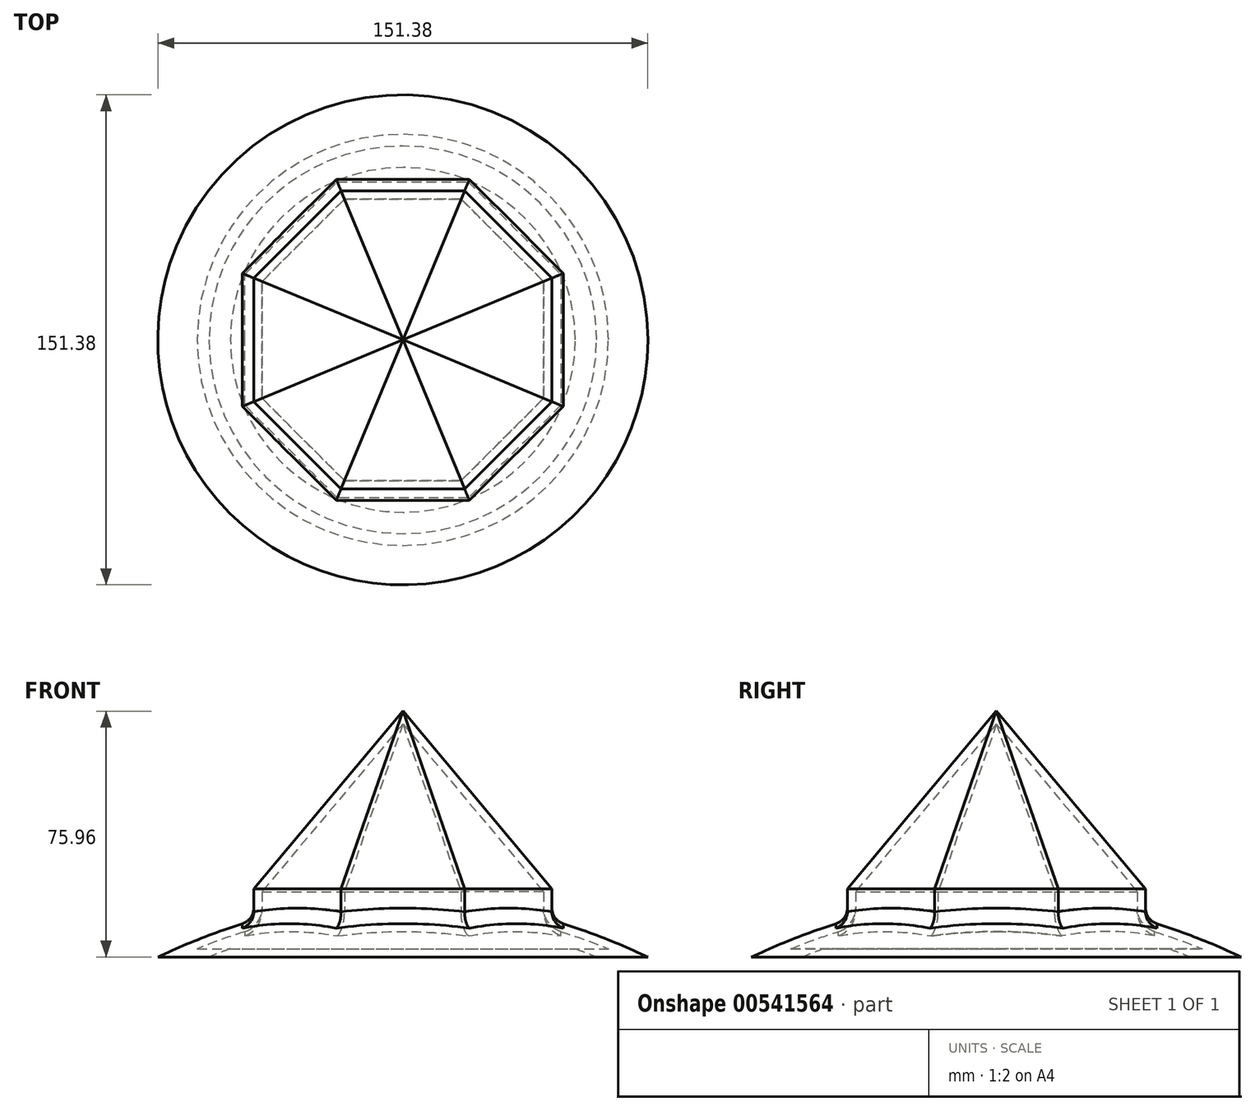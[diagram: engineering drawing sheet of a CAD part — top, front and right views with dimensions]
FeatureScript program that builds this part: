
annotation { "Feature Type Name" : "Feature", "Feature Type Description" : "" }
export const myFeature = defineFeature(function(context is Context, id is Id, definition is map)
    precondition{}
    {
        {
            var Q0;
            Q0=qCreatedBy(makeId("Front.planeOp"),FACE);
            var sketch = newSketch(context, id + "F0", { "sketchPlane" : qUnion([Q0])});
            skArc(sketch, "E0", {"start": v(0, 19.86) * mm, "mid": v(-38.76, 13.4) * mm, "end": v(-75.7, 0) * mm});
            skArc(sketch, "E1", {"start": v(0, 12.95) * mm, "mid": v(-30.5, 9.1) * mm, "end": v(-59.86, 0) * mm});
            skLineSegment(sketch, "E2", {"start": v(-75.7, 0) * mm, "end": v(-59.86, 0) * mm});
            skLineSegment(sketch, "E3", {"start": v(0, 19.86) * mm, "end": v(0, 12.95) * mm});
            skSolve(sketch);
        }
        {
            var Q0;
            Q0=makeQuery(id+"F0.imprint","IMPRINT",FACE,{"disambiguationData":[TD([[makeQuery(id+"F0.imprint","IMPRINT",EDGE,{"derivedFrom":sQuery(id+"F0.wireOp",EDGE,"E0")}),1.0]])]});
            var Q1;
            Q1=sQuery(id+"F0.wireOp",EDGE,"E3");
            revolve(context, id + "F1", {"entities" : qUnion([Q0]), "axis" : qUnion([Q1]), "revolveType" : RevolveType.FULL});
        }
        {
            var Q0;
            Q0=qCreatedBy(makeId("Top.planeOp"),FACE);
            var sketch = newSketch(context, id + "F2", { "sketchPlane" : qUnion([Q0])});
            skCircle(sketch, "E4.cCircle", {"center": v(0, 0) * mm, "radius": 46.05 * mm, "construction": true});
            skLineSegment(sketch, "E4.0", {"start": v(-19.07, 46.05) * mm, "end": v(19.07, 46.05) * mm});
            skLineSegment(sketch, "E4.1", {"start": v(19.07, 46.05) * mm, "end": v(46.05, 19.07) * mm});
            skLineSegment(sketch, "E4.2", {"start": v(46.05, 19.07) * mm, "end": v(46.05, -19.07) * mm});
            skLineSegment(sketch, "E4.3", {"start": v(46.05, -19.07) * mm, "end": v(19.07, -46.05) * mm});
            skLineSegment(sketch, "E4.4", {"start": v(19.07, -46.05) * mm, "end": v(-19.07, -46.05) * mm});
            skLineSegment(sketch, "E4.5", {"start": v(-19.07, -46.05) * mm, "end": v(-46.05, -19.07) * mm});
            skLineSegment(sketch, "E4.6", {"start": v(-46.05, -19.07) * mm, "end": v(-46.05, 19.07) * mm});
            skLineSegment(sketch, "E4.7", {"start": v(-46.05, 19.07) * mm, "end": v(-19.07, 46.05) * mm});
            skPoint(sketch, "E4.0.midPoint", {"position": v(0, 46.05) * mm});
            skSolve(sketch);
        }
        {
            var Q0;
            Q0 = qSketchRegion(id + "F2", true);
            extrude(context, id + "F3", {"entities" : qUnion([Q0]), "operationType" : NewBodyOperationType.ADD, "depth" : 21.08 * mm, "offsetDistance" : 25.4 * mm});
        }
        {
            var Q0;
            Q0=makeQuery(id+"F3.opExtrude","CAP_FACE",FACE,{"disambiguationData":[OSD([sQuery(id+"F2.wireOp",EDGE,"E4.0"),sQuery(id+"F2.wireOp",EDGE,"E4.1"),sQuery(id+"F2.wireOp",EDGE,"E4.2"),sQuery(id+"F2.wireOp",EDGE,"E4.3"),sQuery(id+"F2.wireOp",EDGE,"E4.4"),sQuery(id+"F2.wireOp",EDGE,"E4.5"),sQuery(id+"F2.wireOp",EDGE,"E4.6"),sQuery(id+"F2.wireOp",EDGE,"E4.7")])],"isStart":false});
            extrude(context, id + "F4", {"entities" : qUnion([Q0]), "operationType" : NewBodyOperationType.ADD, "depth" : 101.6 * mm, "offsetDistance" : 25.4 * mm, "hasDraft" : true, "draftAngle" : 40 * degree, "draftPullDirection" : true});
        }
        {
            var Q0;
            Q0=makeQuery(id+"F3.boolean.opBoolean","INTERSECT",EDGE,{"derivedFrom":[makeQuery(id+"F1.opRevolve","SWEPT_FACE",FACE,{"disambiguationData":[OSD([sQuery(id+"F0.wireOp",EDGE,"E0")])]}),makeQuery(id+"F3.opExtrude","SWEPT_FACE",FACE,{"disambiguationData":[OSD([sQuery(id+"F2.wireOp",EDGE,"E4.0")])]})]});
            var Q1;
            Q1=makeQuery(id+"F3.boolean.opBoolean","INTERSECT",EDGE,{"derivedFrom":[makeQuery(id+"F1.opRevolve","SWEPT_FACE",FACE,{"disambiguationData":[OSD([sQuery(id+"F0.wireOp",EDGE,"E0")])]}),makeQuery(id+"F3.opExtrude","SWEPT_FACE",FACE,{"disambiguationData":[OSD([sQuery(id+"F2.wireOp",EDGE,"E4.7")])]})]});
            var Q2;
            Q2=makeQuery(id+"F3.boolean.opBoolean","INTERSECT",EDGE,{"derivedFrom":[makeQuery(id+"F1.opRevolve","SWEPT_FACE",FACE,{"disambiguationData":[OSD([sQuery(id+"F0.wireOp",EDGE,"E0")])]}),makeQuery(id+"F3.opExtrude","SWEPT_FACE",FACE,{"disambiguationData":[OSD([sQuery(id+"F2.wireOp",EDGE,"E4.6")])]})]});
            var Q3;
            Q3=makeQuery(id+"F3.boolean.opBoolean","INTERSECT",EDGE,{"derivedFrom":[makeQuery(id+"F1.opRevolve","SWEPT_FACE",FACE,{"disambiguationData":[OSD([sQuery(id+"F0.wireOp",EDGE,"E0")])]}),makeQuery(id+"F3.opExtrude","SWEPT_FACE",FACE,{"disambiguationData":[OSD([sQuery(id+"F2.wireOp",EDGE,"E4.5")])]})]});
            var Q4;
            Q4=makeQuery(id+"F3.boolean.opBoolean","INTERSECT",EDGE,{"derivedFrom":[makeQuery(id+"F1.opRevolve","SWEPT_FACE",FACE,{"disambiguationData":[OSD([sQuery(id+"F0.wireOp",EDGE,"E0")])]}),makeQuery(id+"F3.opExtrude","SWEPT_FACE",FACE,{"disambiguationData":[OSD([sQuery(id+"F2.wireOp",EDGE,"E4.4")])]})]});
            var Q5;
            Q5=makeQuery(id+"F3.boolean.opBoolean","INTERSECT",EDGE,{"derivedFrom":[makeQuery(id+"F1.opRevolve","SWEPT_FACE",FACE,{"disambiguationData":[OSD([sQuery(id+"F0.wireOp",EDGE,"E0")])]}),makeQuery(id+"F3.opExtrude","SWEPT_FACE",FACE,{"disambiguationData":[OSD([sQuery(id+"F2.wireOp",EDGE,"E4.1")])]})]});
            var Q6;
            Q6=makeQuery(id+"F3.boolean.opBoolean","INTERSECT",EDGE,{"derivedFrom":[makeQuery(id+"F1.opRevolve","SWEPT_FACE",FACE,{"disambiguationData":[OSD([sQuery(id+"F0.wireOp",EDGE,"E0")])]}),makeQuery(id+"F3.opExtrude","SWEPT_FACE",FACE,{"disambiguationData":[OSD([sQuery(id+"F2.wireOp",EDGE,"E4.2")])]})]});
            var Q7;
            Q7=makeQuery(id+"F3.boolean.opBoolean","INTERSECT",EDGE,{"derivedFrom":[makeQuery(id+"F1.opRevolve","SWEPT_FACE",FACE,{"disambiguationData":[OSD([sQuery(id+"F0.wireOp",EDGE,"E0")])]}),makeQuery(id+"F3.opExtrude","SWEPT_FACE",FACE,{"disambiguationData":[OSD([sQuery(id+"F2.wireOp",EDGE,"E4.3")])]})]});
            fillet(context, id + "F5", {"entities" : qUnion([Q0, Q1, Q2, Q3, Q4, Q5, Q6, Q7]), "radius" : 5.08 * mm, "tangentPropagation" : true, "allowEdgeOverflow" : false});
        }
        {
            var Q0;
            Q0=qCreatedBy(makeId("Front.planeOp"),FACE);
            var sketch = newSketch(context, id + "F6", { "sketchPlane" : qUnion([Q0])});
            skArc(sketch, "E5.0", {"start": v(0, 12.95) * mm, "mid": v(-30.5, 9.1) * mm, "end": v(-59.86, 0) * mm});
            skLineSegment(sketch, "E6", {"start": v(0, 12.95) * mm, "end": v(0, 0) * mm});
            skLineSegment(sketch, "E7", {"start": v(0, 0) * mm, "end": v(-59.86, 0) * mm});
            skSolve(sketch);
        }
        {
            var Q0;
            Q0 = qSketchRegion(id + "F6", true);
            var Q1;
            Q1=sQuery(id+"F6.wireOp",EDGE,"E6");
            revolve(context, id + "F7", {"operationType" : NewBodyOperationType.REMOVE, "entities" : qUnion([Q0]), "axis" : qUnion([Q1]), "revolveType" : RevolveType.FULL, "oppositeDirection" : true});
        }
        {
            var Q0;
            Q0=makeQuery(id+"F7.boolean.opBoolean","MERGE",FACE,{"derivedFrom":[makeQuery(id+"F1.opRevolve","SWEPT_FACE",FACE,{"disambiguationData":[OSD([sQuery(id+"F0.wireOp",EDGE,"E1")])]}),makeQuery(id+"F7.opRevolve","SWEPT_FACE",FACE,{"disambiguationData":[OSD([sQuery(id+"F6.wireOp",EDGE,"E5.0")])]})]});
            shell(context, id + "F8", {"entities" : qUnion([Q0]), "thickness" : 2.54 * mm});
        }
    });
